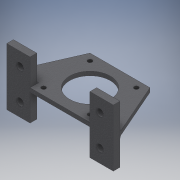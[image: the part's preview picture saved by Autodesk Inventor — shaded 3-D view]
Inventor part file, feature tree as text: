
AUTODESK INVENTOR PART (.ipt)
format: ipt  version: 2018 (Build 220112000, 112)  size: 199,168 bytes
history: native  units: mm
features: extrude x6, sketch x6, thread x4, reference x4, other x3, mirror x1, fillet x1
ambient origin geometry x8: Origin, YZ Plane, XZ Plane, XY Plane, X Axis, Y Axis, Z Axis, Center Point
bodies: Solid1 (feature_tree)
feature tree (25):
  extrude  "Extrusion1"  Depth=90.0mm
  extrude  "Extrusion2"  Depth=40.0mm TaperAngle=0.0deg
  extrude  "Extrusion4"  Depth=6.0mm TaperAngle=0.0deg
  extrude  "Extrusion6"  Depth=10.0mm TaperAngle=0.0deg
  mirror  "Mirror1"
  extrude  "Extrusion9"  Depth=10.0mm TaperAngle=0.0deg
  thread  "Thread10"  [1 undecoded]
  thread  "Thread11"  [1 undecoded]
  thread  "Thread12"  [1 undecoded]
  thread  "Thread13"  [1 undecoded]
  extrude  "Extrusion10"  Depth=3.0mm
  fillet  "Fillet3"  Radius=46.0mm
  sketch  "Sketch1"  dims[d0=90.0mm d1=90.0mm]
  sketch  "Sketch2"  dims[d2=6.0mm d3=0.0mm d14=40.0mm d15=46.0mm d16=0.0mm d17=0.0mm]
  sketch  "Sketch4"  dims[d22=61.0mm d23=6.0mm d24=0.0mm]
  sketch  "Sketch9"  dims[d65=40.0mm d66=0.0mm d88=10.0mm d89=0.0mm]
  sketch  "Sketch12"  dims[d90=10.0mm d91=0.0mm d92=10.0mm d93=0.0mm d94=10.0mm d95=0.0mm d96=10.0mm d97=0.0mm d100=35.0mm d101=10.0mm]
  reference  "Reference5"
  reference  "Reference6"
  reference  "Reference7"
  reference  "Reference8"
  sketch  "Sketch14"  dims[d112=15.0mm d113=20.0mm d114=46.0mm d115=10.5mm d116=10.5mm d117=50.0mm d118=10.0mm d119=0.0mm d120=3.0mm d49=1.0mm d50=1.0mm]
  other  "Z axis motor mount sub-assembly.iam"
  other  "Servo Motor:1"
  other  "Body:1"
note: 4 required parameter values undecoded (feature->parameter linkage not recoverable at this tier; creation-order binding heuristic only, values carry confidence <= 0.55)
